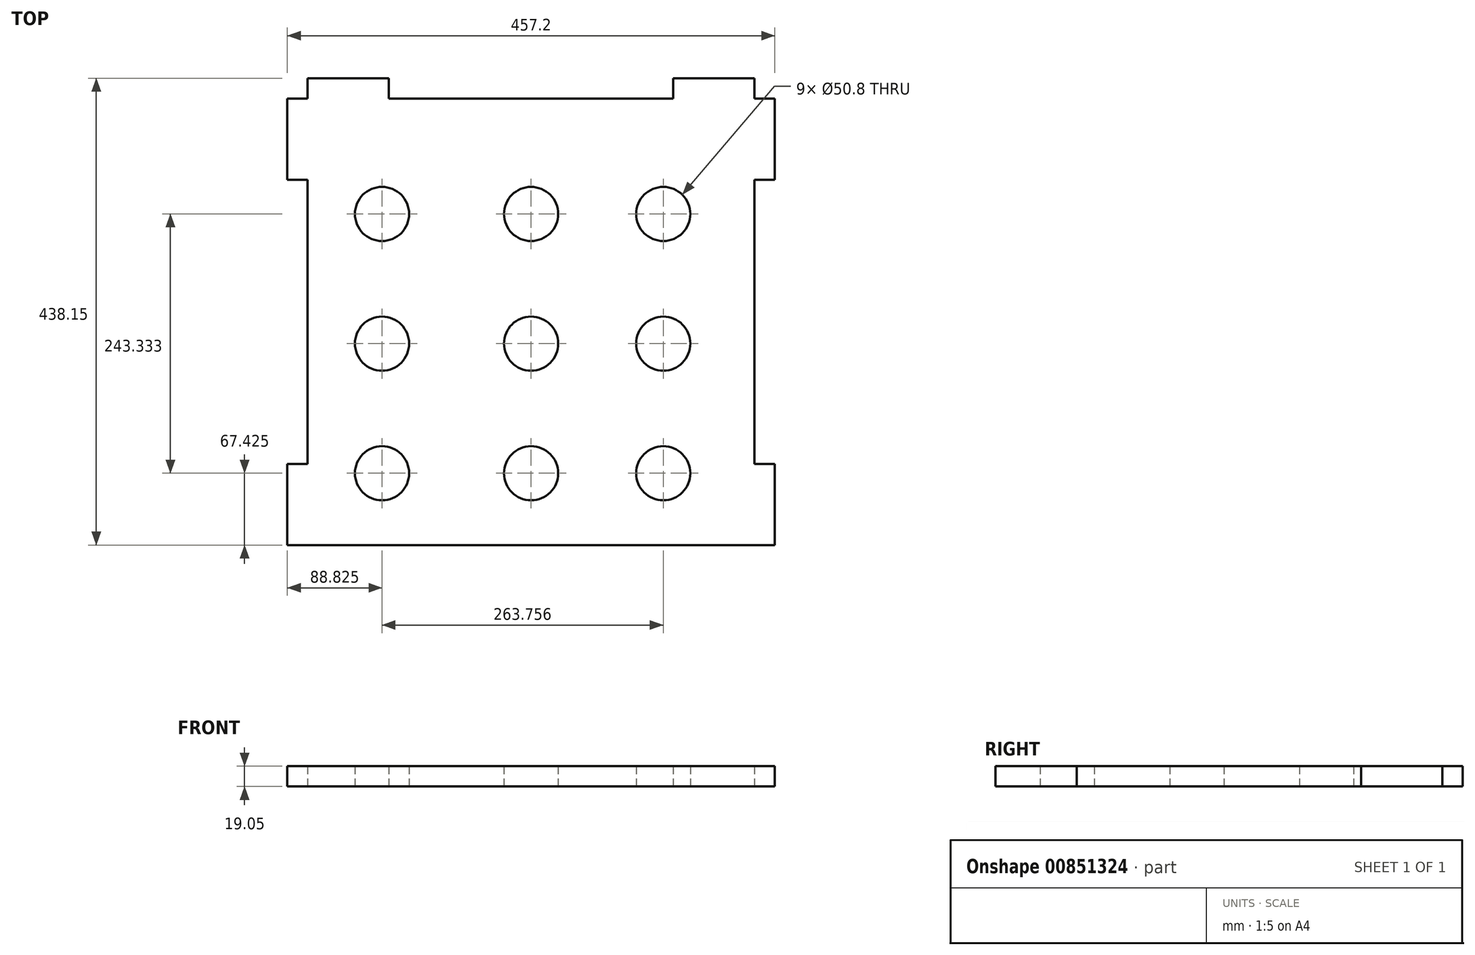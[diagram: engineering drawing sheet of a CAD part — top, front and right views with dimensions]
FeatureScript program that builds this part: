
annotation { "Feature Type Name" : "Feature", "Feature Type Description" : "" }
export const myFeature = defineFeature(function(context is Context, id is Id, definition is map)
    precondition{}
    {
        {
            var Q0;
            Q0=qCreatedBy(makeId("Top.planeOp"),FACE);
            var sketch = newSketch(context, id + "F0", { "sketchPlane" : qUnion([Q0])});
            skLineSegment(sketch, "E0", {"start": v(-215.36, -438.15) * mm, "end": v(203.74, -438.15) * mm});
            skCircle(sketch, "E1", {"center": v(-5.81, -249.06) * mm, "radius": 25.4 * mm});
            skCircle(sketch, "E2", {"center": v(118.17, -249.06) * mm, "radius": 25.4 * mm});
            skCircle(sketch, "E3", {"center": v(-145.59, -249.06) * mm, "radius": 25.4 * mm});
            skCircle(sketch, "E4", {"center": v(-145.59, -127.4) * mm, "radius": 25.4 * mm});
            skCircle(sketch, "E5", {"center": v(-5.81, -127.4) * mm, "radius": 25.4 * mm});
            skCircle(sketch, "E6", {"center": v(118.17, -127.4) * mm, "radius": 25.4 * mm});
            skCircle(sketch, "E7", {"center": v(-5.81, -370.72) * mm, "radius": 25.4 * mm});
            skCircle(sketch, "E8", {"center": v(118.17, -370.72) * mm, "radius": 25.4 * mm});
            skCircle(sketch, "E9", {"center": v(-145.59, -370.72) * mm, "radius": 25.4 * mm});
            skLineSegment(sketch, "E10", {"start": v(-215.36, -438.15) * mm, "end": v(-234.41, -438.15) * mm});
            skLineSegment(sketch, "E11", {"start": v(-234.41, -438.15) * mm, "end": v(-234.41, -361.95) * mm});
            skLineSegment(sketch, "E12", {"start": v(-234.41, -361.95) * mm, "end": v(-215.36, -361.95) * mm});
            skLineSegment(sketch, "E13", {"start": v(-215.36, -19.05) * mm, "end": v(-234.41, -19.05) * mm});
            skLineSegment(sketch, "E14", {"start": v(-234.41, -19.05) * mm, "end": v(-234.41, -95.25) * mm});
            skLineSegment(sketch, "E15", {"start": v(-234.41, -95.25) * mm, "end": v(-215.36, -95.25) * mm});
            skLineSegment(sketch, "E16", {"start": v(-215.36, -361.95) * mm, "end": v(-215.36, -95.25) * mm});
            skLineSegment(sketch, "E17", {"start": v(-215.36, -19.05) * mm, "end": v(-215.36, 0) * mm});
            skLineSegment(sketch, "E18", {"start": v(-215.36, 0) * mm, "end": v(-139.16, 0) * mm});
            skLineSegment(sketch, "E19", {"start": v(-139.16, 0) * mm, "end": v(-139.16, -19.05) * mm});
            skLineSegment(sketch, "E20", {"start": v(203.74, -19.05) * mm, "end": v(203.74, 0) * mm});
            skLineSegment(sketch, "E21", {"start": v(203.74, 0) * mm, "end": v(127.54, 0) * mm});
            skLineSegment(sketch, "E22", {"start": v(127.54, 0) * mm, "end": v(127.54, -19.05) * mm});
            skLineSegment(sketch, "E23", {"start": v(-139.16, -19.05) * mm, "end": v(127.54, -19.05) * mm});
            skLineSegment(sketch, "E24", {"start": v(203.74, -19.05) * mm, "end": v(222.79, -19.05) * mm});
            skLineSegment(sketch, "E25", {"start": v(222.79, -19.05) * mm, "end": v(222.79, -95.25) * mm});
            skLineSegment(sketch, "E26", {"start": v(222.79, -95.25) * mm, "end": v(203.74, -95.25) * mm});
            skLineSegment(sketch, "E27", {"start": v(203.74, -438.15) * mm, "end": v(222.79, -438.15) * mm});
            skLineSegment(sketch, "E28", {"start": v(222.79, -438.15) * mm, "end": v(222.79, -361.95) * mm});
            skLineSegment(sketch, "E29", {"start": v(222.79, -361.95) * mm, "end": v(203.74, -361.95) * mm});
            skLineSegment(sketch, "E30", {"start": v(203.74, -95.25) * mm, "end": v(203.74, -361.95) * mm});
            skSolve(sketch);
        }
        {
            var Q0;
            Q0=makeQuery(id+"F0.imprint","IMPRINT",FACE,{"disambiguationData":[TD([[makeQuery(id+"F0.imprint","IMPRINT",EDGE,{"derivedFrom":sQuery(id+"F0.wireOp",EDGE,"E0")}),1.0]])]});
            extrude(context, id + "F1", {"entities" : qUnion([Q0]), "depth" : 19.05 * mm, "offsetDistance" : 25.4 * mm});
        }
    });
